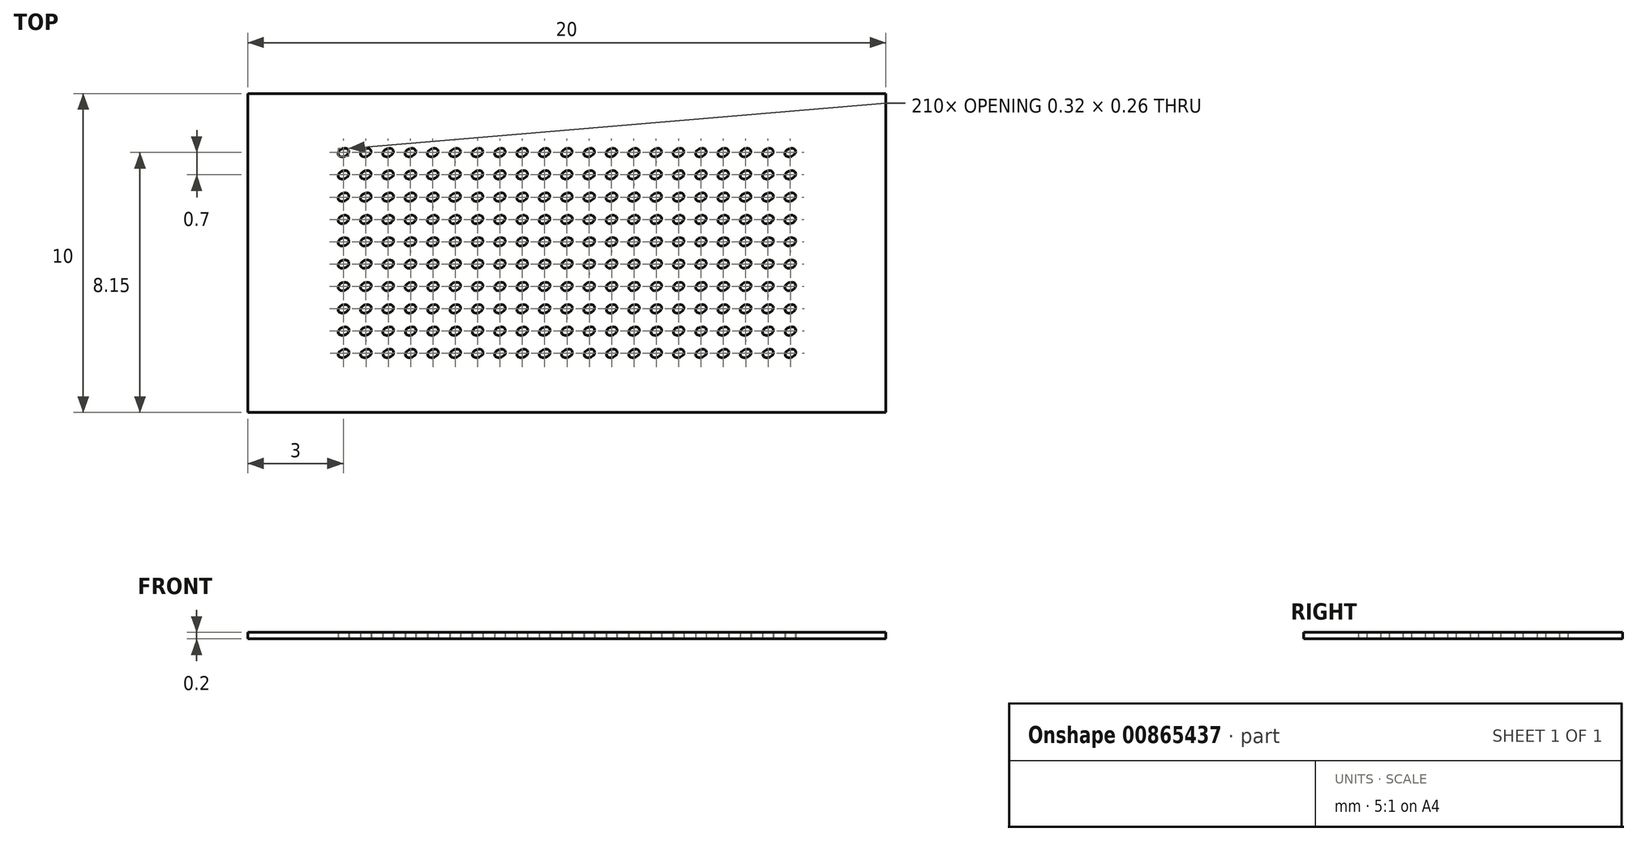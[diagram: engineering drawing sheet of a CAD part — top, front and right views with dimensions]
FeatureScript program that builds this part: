
annotation { "Feature Type Name" : "Feature", "Feature Type Description" : "" }
export const myFeature = defineFeature(function(context is Context, id is Id, definition is map)
    precondition{}
    {
        {
            var Q0;
            Q0=qCreatedBy(makeId("Top.planeOp"),FACE);
            var sketch = newSketch(context, id + "F0", { "sketchPlane" : qUnion([Q0])});
            skLineSegment(sketch, "E0.bottom", {"start": v(0, 0) * mm, "end": v(20, 0) * mm});
            skLineSegment(sketch, "E0.top", {"start": v(0, -10) * mm, "end": v(20, -10) * mm});
            skLineSegment(sketch, "E0.left", {"start": v(0, 0) * mm, "end": v(0, -10) * mm});
            skLineSegment(sketch, "E0.right", {"start": v(20, 0) * mm, "end": v(20, -10) * mm});
            skEllipse(sketch, "E1", {"center": v(3, -1.85) * mm, "majorRadius": 0.17 * mm, "minorRadius": 0.12 * mm, "majorAxis": v(0.93, 0.38)});
            skEllipse(sketch, "E2.1.0.0", {"center": v(3.7, -1.85) * mm, "majorRadius": 0.17 * mm, "minorRadius": 0.12 * mm, "majorAxis": v(0.93, 0.38)});
            skEllipse(sketch, "E2.2.0.0", {"center": v(4.4, -1.85) * mm, "majorRadius": 0.17 * mm, "minorRadius": 0.12 * mm, "majorAxis": v(0.93, 0.38)});
            skLineSegment(sketch, "E2.direction1", {"start": v(3, -1.85) * mm, "end": v(3.7, -1.85) * mm, "construction": true});
            skEllipse(sketch, "E3.0.3.0", {"center": v(5.1, -1.85) * mm, "majorRadius": 0.17 * mm, "minorRadius": 0.12 * mm, "majorAxis": v(0.93, 0.38)});
            skEllipse(sketch, "E3.0.4.0", {"center": v(5.8, -1.85) * mm, "majorRadius": 0.17 * mm, "minorRadius": 0.12 * mm, "majorAxis": v(0.93, 0.38)});
            skEllipse(sketch, "E3.0.5.0", {"center": v(6.5, -1.85) * mm, "majorRadius": 0.17 * mm, "minorRadius": 0.12 * mm, "majorAxis": v(0.93, 0.38)});
            skEllipse(sketch, "E3.0.6.0", {"center": v(7.2, -1.85) * mm, "majorRadius": 0.17 * mm, "minorRadius": 0.12 * mm, "majorAxis": v(0.93, 0.38)});
            skEllipse(sketch, "E3.0.7.0", {"center": v(7.9, -1.85) * mm, "majorRadius": 0.17 * mm, "minorRadius": 0.12 * mm, "majorAxis": v(0.93, 0.38)});
            skEllipse(sketch, "E3.0.8.0", {"center": v(8.6, -1.85) * mm, "majorRadius": 0.17 * mm, "minorRadius": 0.12 * mm, "majorAxis": v(0.93, 0.38)});
            skEllipse(sketch, "E3.0.9.0", {"center": v(9.3, -1.85) * mm, "majorRadius": 0.17 * mm, "minorRadius": 0.12 * mm, "majorAxis": v(0.93, 0.38)});
            skEllipse(sketch, "E3.0.10.0", {"center": v(10, -1.85) * mm, "majorRadius": 0.17 * mm, "minorRadius": 0.12 * mm, "majorAxis": v(0.93, 0.38)});
            skEllipse(sketch, "E3.0.11.0", {"center": v(10.7, -1.85) * mm, "majorRadius": 0.17 * mm, "minorRadius": 0.12 * mm, "majorAxis": v(0.93, 0.38)});
            skEllipse(sketch, "E3.0.12.0", {"center": v(11.4, -1.85) * mm, "majorRadius": 0.17 * mm, "minorRadius": 0.12 * mm, "majorAxis": v(0.93, 0.38)});
            skEllipse(sketch, "E3.0.13.0", {"center": v(12.1, -1.85) * mm, "majorRadius": 0.17 * mm, "minorRadius": 0.12 * mm, "majorAxis": v(0.93, 0.38)});
            skEllipse(sketch, "E3.0.14.0", {"center": v(12.8, -1.85) * mm, "majorRadius": 0.17 * mm, "minorRadius": 0.12 * mm, "majorAxis": v(0.93, 0.38)});
            skEllipse(sketch, "E3.0.15.0", {"center": v(13.5, -1.85) * mm, "majorRadius": 0.17 * mm, "minorRadius": 0.12 * mm, "majorAxis": v(0.93, 0.38)});
            skEllipse(sketch, "E3.0.16.0", {"center": v(14.2, -1.85) * mm, "majorRadius": 0.17 * mm, "minorRadius": 0.12 * mm, "majorAxis": v(0.93, 0.38)});
            skEllipse(sketch, "E3.0.17.0", {"center": v(14.9, -1.85) * mm, "majorRadius": 0.17 * mm, "minorRadius": 0.12 * mm, "majorAxis": v(0.93, 0.38)});
            skEllipse(sketch, "E3.0.18.0", {"center": v(15.6, -1.85) * mm, "majorRadius": 0.17 * mm, "minorRadius": 0.12 * mm, "majorAxis": v(0.93, 0.38)});
            skEllipse(sketch, "E3.0.19.0", {"center": v(16.3, -1.85) * mm, "majorRadius": 0.17 * mm, "minorRadius": 0.12 * mm, "majorAxis": v(0.93, 0.38)});
            skEllipse(sketch, "E4.0.20.0", {"center": v(17, -1.85) * mm, "majorRadius": 0.17 * mm, "minorRadius": 0.12 * mm, "majorAxis": v(0.93, 0.38)});
            skEllipse(sketch, "E5.1.0.0", {"center": v(17, -2.55) * mm, "majorRadius": 0.17 * mm, "minorRadius": 0.12 * mm, "majorAxis": v(0.93, 0.38)});
            skEllipse(sketch, "E5.1.0.1", {"center": v(16.3, -2.55) * mm, "majorRadius": 0.17 * mm, "minorRadius": 0.12 * mm, "majorAxis": v(0.93, 0.38)});
            skEllipse(sketch, "E5.1.0.2", {"center": v(15.6, -2.55) * mm, "majorRadius": 0.17 * mm, "minorRadius": 0.12 * mm, "majorAxis": v(0.93, 0.38)});
            skEllipse(sketch, "E5.1.0.3", {"center": v(14.9, -2.55) * mm, "majorRadius": 0.17 * mm, "minorRadius": 0.12 * mm, "majorAxis": v(0.93, 0.38)});
            skEllipse(sketch, "E5.1.0.4", {"center": v(14.2, -2.55) * mm, "majorRadius": 0.17 * mm, "minorRadius": 0.12 * mm, "majorAxis": v(0.93, 0.38)});
            skEllipse(sketch, "E5.1.0.5", {"center": v(13.5, -2.55) * mm, "majorRadius": 0.17 * mm, "minorRadius": 0.12 * mm, "majorAxis": v(0.93, 0.38)});
            skEllipse(sketch, "E5.1.0.6", {"center": v(12.8, -2.55) * mm, "majorRadius": 0.17 * mm, "minorRadius": 0.12 * mm, "majorAxis": v(0.93, 0.38)});
            skEllipse(sketch, "E5.1.0.7", {"center": v(12.1, -2.55) * mm, "majorRadius": 0.17 * mm, "minorRadius": 0.12 * mm, "majorAxis": v(0.93, 0.38)});
            skEllipse(sketch, "E5.1.0.8", {"center": v(11.4, -2.55) * mm, "majorRadius": 0.17 * mm, "minorRadius": 0.12 * mm, "majorAxis": v(0.93, 0.38)});
            skEllipse(sketch, "E5.1.0.9", {"center": v(10.7, -2.55) * mm, "majorRadius": 0.17 * mm, "minorRadius": 0.12 * mm, "majorAxis": v(0.93, 0.38)});
            skEllipse(sketch, "E5.1.0.10", {"center": v(10, -2.55) * mm, "majorRadius": 0.17 * mm, "minorRadius": 0.12 * mm, "majorAxis": v(0.93, 0.38)});
            skEllipse(sketch, "E5.1.0.11", {"center": v(9.3, -2.55) * mm, "majorRadius": 0.17 * mm, "minorRadius": 0.12 * mm, "majorAxis": v(0.93, 0.38)});
            skEllipse(sketch, "E5.1.0.12", {"center": v(8.6, -2.55) * mm, "majorRadius": 0.17 * mm, "minorRadius": 0.12 * mm, "majorAxis": v(0.93, 0.38)});
            skEllipse(sketch, "E5.1.0.13", {"center": v(7.9, -2.55) * mm, "majorRadius": 0.17 * mm, "minorRadius": 0.12 * mm, "majorAxis": v(0.93, 0.38)});
            skEllipse(sketch, "E5.1.0.14", {"center": v(7.2, -2.55) * mm, "majorRadius": 0.17 * mm, "minorRadius": 0.12 * mm, "majorAxis": v(0.93, 0.38)});
            skEllipse(sketch, "E5.1.0.15", {"center": v(5.8, -2.55) * mm, "majorRadius": 0.17 * mm, "minorRadius": 0.12 * mm, "majorAxis": v(0.93, 0.38)});
            skEllipse(sketch, "E5.1.0.16", {"center": v(5.1, -2.55) * mm, "majorRadius": 0.17 * mm, "minorRadius": 0.12 * mm, "majorAxis": v(0.93, 0.38)});
            skEllipse(sketch, "E5.1.0.17", {"center": v(6.5, -2.55) * mm, "majorRadius": 0.17 * mm, "minorRadius": 0.12 * mm, "majorAxis": v(0.93, 0.38)});
            skEllipse(sketch, "E5.1.0.18", {"center": v(4.4, -2.55) * mm, "majorRadius": 0.17 * mm, "minorRadius": 0.12 * mm, "majorAxis": v(0.93, 0.38)});
            skEllipse(sketch, "E5.1.0.19", {"center": v(3.7, -2.55) * mm, "majorRadius": 0.17 * mm, "minorRadius": 0.12 * mm, "majorAxis": v(0.93, 0.38)});
            skEllipse(sketch, "E5.1.0.20", {"center": v(3, -2.55) * mm, "majorRadius": 0.17 * mm, "minorRadius": 0.12 * mm, "majorAxis": v(0.93, 0.38)});
            skEllipse(sketch, "E5.2.0.0", {"center": v(17, -3.25) * mm, "majorRadius": 0.17 * mm, "minorRadius": 0.12 * mm, "majorAxis": v(0.93, 0.38)});
            skEllipse(sketch, "E5.2.0.1", {"center": v(16.3, -3.25) * mm, "majorRadius": 0.17 * mm, "minorRadius": 0.12 * mm, "majorAxis": v(0.93, 0.38)});
            skEllipse(sketch, "E5.2.0.2", {"center": v(15.6, -3.25) * mm, "majorRadius": 0.17 * mm, "minorRadius": 0.12 * mm, "majorAxis": v(0.93, 0.38)});
            skEllipse(sketch, "E5.2.0.3", {"center": v(14.9, -3.25) * mm, "majorRadius": 0.17 * mm, "minorRadius": 0.12 * mm, "majorAxis": v(0.93, 0.38)});
            skEllipse(sketch, "E5.2.0.4", {"center": v(14.2, -3.25) * mm, "majorRadius": 0.17 * mm, "minorRadius": 0.12 * mm, "majorAxis": v(0.93, 0.38)});
            skEllipse(sketch, "E5.2.0.5", {"center": v(13.5, -3.25) * mm, "majorRadius": 0.17 * mm, "minorRadius": 0.12 * mm, "majorAxis": v(0.93, 0.38)});
            skEllipse(sketch, "E5.2.0.6", {"center": v(12.8, -3.25) * mm, "majorRadius": 0.17 * mm, "minorRadius": 0.12 * mm, "majorAxis": v(0.93, 0.38)});
            skEllipse(sketch, "E5.2.0.7", {"center": v(12.1, -3.25) * mm, "majorRadius": 0.17 * mm, "minorRadius": 0.12 * mm, "majorAxis": v(0.93, 0.38)});
            skEllipse(sketch, "E5.2.0.8", {"center": v(11.4, -3.25) * mm, "majorRadius": 0.17 * mm, "minorRadius": 0.12 * mm, "majorAxis": v(0.93, 0.38)});
            skEllipse(sketch, "E5.2.0.9", {"center": v(10.7, -3.25) * mm, "majorRadius": 0.17 * mm, "minorRadius": 0.12 * mm, "majorAxis": v(0.93, 0.38)});
            skEllipse(sketch, "E5.2.0.10", {"center": v(10, -3.25) * mm, "majorRadius": 0.17 * mm, "minorRadius": 0.12 * mm, "majorAxis": v(0.93, 0.38)});
            skEllipse(sketch, "E5.2.0.11", {"center": v(9.3, -3.25) * mm, "majorRadius": 0.17 * mm, "minorRadius": 0.12 * mm, "majorAxis": v(0.93, 0.38)});
            skEllipse(sketch, "E5.2.0.12", {"center": v(8.6, -3.25) * mm, "majorRadius": 0.17 * mm, "minorRadius": 0.12 * mm, "majorAxis": v(0.93, 0.38)});
            skEllipse(sketch, "E5.2.0.13", {"center": v(7.9, -3.25) * mm, "majorRadius": 0.17 * mm, "minorRadius": 0.12 * mm, "majorAxis": v(0.93, 0.38)});
            skEllipse(sketch, "E5.2.0.14", {"center": v(7.2, -3.25) * mm, "majorRadius": 0.17 * mm, "minorRadius": 0.12 * mm, "majorAxis": v(0.93, 0.38)});
            skEllipse(sketch, "E5.2.0.15", {"center": v(5.8, -3.25) * mm, "majorRadius": 0.17 * mm, "minorRadius": 0.12 * mm, "majorAxis": v(0.93, 0.38)});
            skEllipse(sketch, "E5.2.0.16", {"center": v(5.1, -3.25) * mm, "majorRadius": 0.17 * mm, "minorRadius": 0.12 * mm, "majorAxis": v(0.93, 0.38)});
            skEllipse(sketch, "E5.2.0.17", {"center": v(6.5, -3.25) * mm, "majorRadius": 0.17 * mm, "minorRadius": 0.12 * mm, "majorAxis": v(0.93, 0.38)});
            skEllipse(sketch, "E5.2.0.18", {"center": v(4.4, -3.25) * mm, "majorRadius": 0.17 * mm, "minorRadius": 0.12 * mm, "majorAxis": v(0.93, 0.38)});
            skEllipse(sketch, "E5.2.0.19", {"center": v(3.7, -3.25) * mm, "majorRadius": 0.17 * mm, "minorRadius": 0.12 * mm, "majorAxis": v(0.93, 0.38)});
            skEllipse(sketch, "E5.2.0.20", {"center": v(3, -3.25) * mm, "majorRadius": 0.17 * mm, "minorRadius": 0.12 * mm, "majorAxis": v(0.93, 0.38)});
            skEllipse(sketch, "E5.3.0.0", {"center": v(17, -3.95) * mm, "majorRadius": 0.17 * mm, "minorRadius": 0.12 * mm, "majorAxis": v(0.93, 0.38)});
            skEllipse(sketch, "E5.3.0.1", {"center": v(16.3, -3.95) * mm, "majorRadius": 0.17 * mm, "minorRadius": 0.12 * mm, "majorAxis": v(0.93, 0.38)});
            skEllipse(sketch, "E5.3.0.2", {"center": v(15.6, -3.95) * mm, "majorRadius": 0.17 * mm, "minorRadius": 0.12 * mm, "majorAxis": v(0.93, 0.38)});
            skEllipse(sketch, "E5.3.0.3", {"center": v(14.9, -3.95) * mm, "majorRadius": 0.17 * mm, "minorRadius": 0.12 * mm, "majorAxis": v(0.93, 0.38)});
            skEllipse(sketch, "E5.3.0.4", {"center": v(14.2, -3.95) * mm, "majorRadius": 0.17 * mm, "minorRadius": 0.12 * mm, "majorAxis": v(0.93, 0.38)});
            skEllipse(sketch, "E5.3.0.5", {"center": v(13.5, -3.95) * mm, "majorRadius": 0.17 * mm, "minorRadius": 0.12 * mm, "majorAxis": v(0.93, 0.38)});
            skEllipse(sketch, "E5.3.0.6", {"center": v(12.8, -3.95) * mm, "majorRadius": 0.17 * mm, "minorRadius": 0.12 * mm, "majorAxis": v(0.93, 0.38)});
            skEllipse(sketch, "E5.3.0.7", {"center": v(12.1, -3.95) * mm, "majorRadius": 0.17 * mm, "minorRadius": 0.12 * mm, "majorAxis": v(0.93, 0.38)});
            skEllipse(sketch, "E5.3.0.8", {"center": v(11.4, -3.95) * mm, "majorRadius": 0.17 * mm, "minorRadius": 0.12 * mm, "majorAxis": v(0.93, 0.38)});
            skEllipse(sketch, "E5.3.0.9", {"center": v(10.7, -3.95) * mm, "majorRadius": 0.17 * mm, "minorRadius": 0.12 * mm, "majorAxis": v(0.93, 0.38)});
            skEllipse(sketch, "E5.3.0.10", {"center": v(10, -3.95) * mm, "majorRadius": 0.17 * mm, "minorRadius": 0.12 * mm, "majorAxis": v(0.93, 0.38)});
            skEllipse(sketch, "E5.3.0.11", {"center": v(9.3, -3.95) * mm, "majorRadius": 0.17 * mm, "minorRadius": 0.12 * mm, "majorAxis": v(0.93, 0.38)});
            skEllipse(sketch, "E5.3.0.12", {"center": v(8.6, -3.95) * mm, "majorRadius": 0.17 * mm, "minorRadius": 0.12 * mm, "majorAxis": v(0.93, 0.38)});
            skEllipse(sketch, "E5.3.0.13", {"center": v(7.9, -3.95) * mm, "majorRadius": 0.17 * mm, "minorRadius": 0.12 * mm, "majorAxis": v(0.93, 0.38)});
            skEllipse(sketch, "E5.3.0.14", {"center": v(7.2, -3.95) * mm, "majorRadius": 0.17 * mm, "minorRadius": 0.12 * mm, "majorAxis": v(0.93, 0.38)});
            skEllipse(sketch, "E5.3.0.15", {"center": v(5.8, -3.95) * mm, "majorRadius": 0.17 * mm, "minorRadius": 0.12 * mm, "majorAxis": v(0.93, 0.38)});
            skEllipse(sketch, "E5.3.0.16", {"center": v(5.1, -3.95) * mm, "majorRadius": 0.17 * mm, "minorRadius": 0.12 * mm, "majorAxis": v(0.93, 0.38)});
            skEllipse(sketch, "E5.3.0.17", {"center": v(6.5, -3.95) * mm, "majorRadius": 0.17 * mm, "minorRadius": 0.12 * mm, "majorAxis": v(0.93, 0.38)});
            skEllipse(sketch, "E5.3.0.18", {"center": v(4.4, -3.95) * mm, "majorRadius": 0.17 * mm, "minorRadius": 0.12 * mm, "majorAxis": v(0.93, 0.38)});
            skEllipse(sketch, "E5.3.0.19", {"center": v(3.7, -3.95) * mm, "majorRadius": 0.17 * mm, "minorRadius": 0.12 * mm, "majorAxis": v(0.93, 0.38)});
            skEllipse(sketch, "E5.3.0.20", {"center": v(3, -3.95) * mm, "majorRadius": 0.17 * mm, "minorRadius": 0.12 * mm, "majorAxis": v(0.93, 0.38)});
            skEllipse(sketch, "E5.4.0.0", {"center": v(17, -4.65) * mm, "majorRadius": 0.17 * mm, "minorRadius": 0.12 * mm, "majorAxis": v(0.93, 0.38)});
            skEllipse(sketch, "E5.4.0.1", {"center": v(16.3, -4.65) * mm, "majorRadius": 0.17 * mm, "minorRadius": 0.12 * mm, "majorAxis": v(0.93, 0.38)});
            skEllipse(sketch, "E5.4.0.2", {"center": v(15.6, -4.65) * mm, "majorRadius": 0.17 * mm, "minorRadius": 0.12 * mm, "majorAxis": v(0.93, 0.38)});
            skEllipse(sketch, "E5.4.0.3", {"center": v(14.9, -4.65) * mm, "majorRadius": 0.17 * mm, "minorRadius": 0.12 * mm, "majorAxis": v(0.93, 0.38)});
            skEllipse(sketch, "E5.4.0.4", {"center": v(14.2, -4.65) * mm, "majorRadius": 0.17 * mm, "minorRadius": 0.12 * mm, "majorAxis": v(0.93, 0.38)});
            skEllipse(sketch, "E5.4.0.5", {"center": v(13.5, -4.65) * mm, "majorRadius": 0.17 * mm, "minorRadius": 0.12 * mm, "majorAxis": v(0.93, 0.38)});
            skEllipse(sketch, "E5.4.0.6", {"center": v(12.8, -4.65) * mm, "majorRadius": 0.17 * mm, "minorRadius": 0.12 * mm, "majorAxis": v(0.93, 0.38)});
            skEllipse(sketch, "E5.4.0.7", {"center": v(12.1, -4.65) * mm, "majorRadius": 0.17 * mm, "minorRadius": 0.12 * mm, "majorAxis": v(0.93, 0.38)});
            skEllipse(sketch, "E5.4.0.8", {"center": v(11.4, -4.65) * mm, "majorRadius": 0.17 * mm, "minorRadius": 0.12 * mm, "majorAxis": v(0.93, 0.38)});
            skEllipse(sketch, "E5.4.0.9", {"center": v(10.7, -4.65) * mm, "majorRadius": 0.17 * mm, "minorRadius": 0.12 * mm, "majorAxis": v(0.93, 0.38)});
            skEllipse(sketch, "E5.4.0.10", {"center": v(10, -4.65) * mm, "majorRadius": 0.17 * mm, "minorRadius": 0.12 * mm, "majorAxis": v(0.93, 0.38)});
            skEllipse(sketch, "E5.4.0.11", {"center": v(9.3, -4.65) * mm, "majorRadius": 0.17 * mm, "minorRadius": 0.12 * mm, "majorAxis": v(0.93, 0.38)});
            skEllipse(sketch, "E5.4.0.12", {"center": v(8.6, -4.65) * mm, "majorRadius": 0.17 * mm, "minorRadius": 0.12 * mm, "majorAxis": v(0.93, 0.38)});
            skEllipse(sketch, "E5.4.0.13", {"center": v(7.9, -4.65) * mm, "majorRadius": 0.17 * mm, "minorRadius": 0.12 * mm, "majorAxis": v(0.93, 0.38)});
            skEllipse(sketch, "E5.4.0.14", {"center": v(7.2, -4.65) * mm, "majorRadius": 0.17 * mm, "minorRadius": 0.12 * mm, "majorAxis": v(0.93, 0.38)});
            skEllipse(sketch, "E5.4.0.15", {"center": v(5.8, -4.65) * mm, "majorRadius": 0.17 * mm, "minorRadius": 0.12 * mm, "majorAxis": v(0.93, 0.38)});
            skEllipse(sketch, "E5.4.0.16", {"center": v(5.1, -4.65) * mm, "majorRadius": 0.17 * mm, "minorRadius": 0.12 * mm, "majorAxis": v(0.93, 0.38)});
            skEllipse(sketch, "E5.4.0.17", {"center": v(6.5, -4.65) * mm, "majorRadius": 0.17 * mm, "minorRadius": 0.12 * mm, "majorAxis": v(0.93, 0.38)});
            skEllipse(sketch, "E5.4.0.18", {"center": v(4.4, -4.65) * mm, "majorRadius": 0.17 * mm, "minorRadius": 0.12 * mm, "majorAxis": v(0.93, 0.38)});
            skEllipse(sketch, "E5.4.0.19", {"center": v(3.7, -4.65) * mm, "majorRadius": 0.17 * mm, "minorRadius": 0.12 * mm, "majorAxis": v(0.93, 0.38)});
            skEllipse(sketch, "E5.4.0.20", {"center": v(3, -4.65) * mm, "majorRadius": 0.17 * mm, "minorRadius": 0.12 * mm, "majorAxis": v(0.93, 0.38)});
            skEllipse(sketch, "E5.5.0.0", {"center": v(17, -5.35) * mm, "majorRadius": 0.17 * mm, "minorRadius": 0.12 * mm, "majorAxis": v(0.93, 0.38)});
            skEllipse(sketch, "E5.5.0.1", {"center": v(16.3, -5.35) * mm, "majorRadius": 0.17 * mm, "minorRadius": 0.12 * mm, "majorAxis": v(0.93, 0.38)});
            skEllipse(sketch, "E5.5.0.2", {"center": v(15.6, -5.35) * mm, "majorRadius": 0.17 * mm, "minorRadius": 0.12 * mm, "majorAxis": v(0.93, 0.38)});
            skEllipse(sketch, "E5.5.0.3", {"center": v(14.9, -5.35) * mm, "majorRadius": 0.17 * mm, "minorRadius": 0.12 * mm, "majorAxis": v(0.93, 0.38)});
            skEllipse(sketch, "E5.5.0.4", {"center": v(14.2, -5.35) * mm, "majorRadius": 0.17 * mm, "minorRadius": 0.12 * mm, "majorAxis": v(0.93, 0.38)});
            skEllipse(sketch, "E5.5.0.5", {"center": v(13.5, -5.35) * mm, "majorRadius": 0.17 * mm, "minorRadius": 0.12 * mm, "majorAxis": v(0.93, 0.38)});
            skEllipse(sketch, "E5.5.0.6", {"center": v(12.8, -5.35) * mm, "majorRadius": 0.17 * mm, "minorRadius": 0.12 * mm, "majorAxis": v(0.93, 0.38)});
            skEllipse(sketch, "E5.5.0.7", {"center": v(12.1, -5.35) * mm, "majorRadius": 0.17 * mm, "minorRadius": 0.12 * mm, "majorAxis": v(0.93, 0.38)});
            skEllipse(sketch, "E5.5.0.8", {"center": v(11.4, -5.35) * mm, "majorRadius": 0.17 * mm, "minorRadius": 0.12 * mm, "majorAxis": v(0.93, 0.38)});
            skEllipse(sketch, "E5.5.0.9", {"center": v(10.7, -5.35) * mm, "majorRadius": 0.17 * mm, "minorRadius": 0.12 * mm, "majorAxis": v(0.93, 0.38)});
            skEllipse(sketch, "E5.5.0.10", {"center": v(10, -5.35) * mm, "majorRadius": 0.17 * mm, "minorRadius": 0.12 * mm, "majorAxis": v(0.93, 0.38)});
            skEllipse(sketch, "E5.5.0.11", {"center": v(9.3, -5.35) * mm, "majorRadius": 0.17 * mm, "minorRadius": 0.12 * mm, "majorAxis": v(0.93, 0.38)});
            skEllipse(sketch, "E5.5.0.12", {"center": v(8.6, -5.35) * mm, "majorRadius": 0.17 * mm, "minorRadius": 0.12 * mm, "majorAxis": v(0.93, 0.38)});
            skEllipse(sketch, "E5.5.0.13", {"center": v(7.9, -5.35) * mm, "majorRadius": 0.17 * mm, "minorRadius": 0.12 * mm, "majorAxis": v(0.93, 0.38)});
            skEllipse(sketch, "E5.5.0.14", {"center": v(7.2, -5.35) * mm, "majorRadius": 0.17 * mm, "minorRadius": 0.12 * mm, "majorAxis": v(0.93, 0.38)});
            skEllipse(sketch, "E5.5.0.15", {"center": v(5.8, -5.35) * mm, "majorRadius": 0.17 * mm, "minorRadius": 0.12 * mm, "majorAxis": v(0.93, 0.38)});
            skEllipse(sketch, "E5.5.0.16", {"center": v(5.1, -5.35) * mm, "majorRadius": 0.17 * mm, "minorRadius": 0.12 * mm, "majorAxis": v(0.93, 0.38)});
            skEllipse(sketch, "E5.5.0.17", {"center": v(6.5, -5.35) * mm, "majorRadius": 0.17 * mm, "minorRadius": 0.12 * mm, "majorAxis": v(0.93, 0.38)});
            skEllipse(sketch, "E5.5.0.18", {"center": v(4.4, -5.35) * mm, "majorRadius": 0.17 * mm, "minorRadius": 0.12 * mm, "majorAxis": v(0.93, 0.38)});
            skEllipse(sketch, "E5.5.0.19", {"center": v(3.7, -5.35) * mm, "majorRadius": 0.17 * mm, "minorRadius": 0.12 * mm, "majorAxis": v(0.93, 0.38)});
            skEllipse(sketch, "E5.5.0.20", {"center": v(3, -5.35) * mm, "majorRadius": 0.17 * mm, "minorRadius": 0.12 * mm, "majorAxis": v(0.93, 0.38)});
            skEllipse(sketch, "E5.6.0.0", {"center": v(17, -6.05) * mm, "majorRadius": 0.17 * mm, "minorRadius": 0.12 * mm, "majorAxis": v(0.93, 0.38)});
            skEllipse(sketch, "E5.6.0.1", {"center": v(16.3, -6.05) * mm, "majorRadius": 0.17 * mm, "minorRadius": 0.12 * mm, "majorAxis": v(0.93, 0.38)});
            skEllipse(sketch, "E5.6.0.2", {"center": v(15.6, -6.05) * mm, "majorRadius": 0.17 * mm, "minorRadius": 0.12 * mm, "majorAxis": v(0.93, 0.38)});
            skEllipse(sketch, "E5.6.0.3", {"center": v(14.9, -6.05) * mm, "majorRadius": 0.17 * mm, "minorRadius": 0.12 * mm, "majorAxis": v(0.93, 0.38)});
            skEllipse(sketch, "E5.6.0.4", {"center": v(14.2, -6.05) * mm, "majorRadius": 0.17 * mm, "minorRadius": 0.12 * mm, "majorAxis": v(0.93, 0.38)});
            skEllipse(sketch, "E5.6.0.5", {"center": v(13.5, -6.05) * mm, "majorRadius": 0.17 * mm, "minorRadius": 0.12 * mm, "majorAxis": v(0.93, 0.38)});
            skEllipse(sketch, "E5.6.0.6", {"center": v(12.8, -6.05) * mm, "majorRadius": 0.17 * mm, "minorRadius": 0.12 * mm, "majorAxis": v(0.93, 0.38)});
            skEllipse(sketch, "E5.6.0.7", {"center": v(12.1, -6.05) * mm, "majorRadius": 0.17 * mm, "minorRadius": 0.12 * mm, "majorAxis": v(0.93, 0.38)});
            skEllipse(sketch, "E5.6.0.8", {"center": v(11.4, -6.05) * mm, "majorRadius": 0.17 * mm, "minorRadius": 0.12 * mm, "majorAxis": v(0.93, 0.38)});
            skEllipse(sketch, "E5.6.0.9", {"center": v(10.7, -6.05) * mm, "majorRadius": 0.17 * mm, "minorRadius": 0.12 * mm, "majorAxis": v(0.93, 0.38)});
            skEllipse(sketch, "E5.6.0.10", {"center": v(10, -6.05) * mm, "majorRadius": 0.17 * mm, "minorRadius": 0.12 * mm, "majorAxis": v(0.93, 0.38)});
            skEllipse(sketch, "E5.6.0.11", {"center": v(9.3, -6.05) * mm, "majorRadius": 0.17 * mm, "minorRadius": 0.12 * mm, "majorAxis": v(0.93, 0.38)});
            skEllipse(sketch, "E5.6.0.12", {"center": v(8.6, -6.05) * mm, "majorRadius": 0.17 * mm, "minorRadius": 0.12 * mm, "majorAxis": v(0.93, 0.38)});
            skEllipse(sketch, "E5.6.0.13", {"center": v(7.9, -6.05) * mm, "majorRadius": 0.17 * mm, "minorRadius": 0.12 * mm, "majorAxis": v(0.93, 0.38)});
            skEllipse(sketch, "E5.6.0.14", {"center": v(7.2, -6.05) * mm, "majorRadius": 0.17 * mm, "minorRadius": 0.12 * mm, "majorAxis": v(0.93, 0.38)});
            skEllipse(sketch, "E5.6.0.15", {"center": v(5.8, -6.05) * mm, "majorRadius": 0.17 * mm, "minorRadius": 0.12 * mm, "majorAxis": v(0.93, 0.38)});
            skEllipse(sketch, "E5.6.0.16", {"center": v(5.1, -6.05) * mm, "majorRadius": 0.17 * mm, "minorRadius": 0.12 * mm, "majorAxis": v(0.93, 0.38)});
            skEllipse(sketch, "E5.6.0.17", {"center": v(6.5, -6.05) * mm, "majorRadius": 0.17 * mm, "minorRadius": 0.12 * mm, "majorAxis": v(0.93, 0.38)});
            skEllipse(sketch, "E5.6.0.18", {"center": v(4.4, -6.05) * mm, "majorRadius": 0.17 * mm, "minorRadius": 0.12 * mm, "majorAxis": v(0.93, 0.38)});
            skEllipse(sketch, "E5.6.0.19", {"center": v(3.7, -6.05) * mm, "majorRadius": 0.17 * mm, "minorRadius": 0.12 * mm, "majorAxis": v(0.93, 0.38)});
            skEllipse(sketch, "E5.6.0.20", {"center": v(3, -6.05) * mm, "majorRadius": 0.17 * mm, "minorRadius": 0.12 * mm, "majorAxis": v(0.93, 0.38)});
            skEllipse(sketch, "E5.7.0.0", {"center": v(17, -6.75) * mm, "majorRadius": 0.17 * mm, "minorRadius": 0.12 * mm, "majorAxis": v(0.93, 0.38)});
            skEllipse(sketch, "E5.7.0.1", {"center": v(16.3, -6.75) * mm, "majorRadius": 0.17 * mm, "minorRadius": 0.12 * mm, "majorAxis": v(0.93, 0.38)});
            skEllipse(sketch, "E5.7.0.2", {"center": v(15.6, -6.75) * mm, "majorRadius": 0.17 * mm, "minorRadius": 0.12 * mm, "majorAxis": v(0.93, 0.38)});
            skEllipse(sketch, "E5.7.0.3", {"center": v(14.9, -6.75) * mm, "majorRadius": 0.17 * mm, "minorRadius": 0.12 * mm, "majorAxis": v(0.93, 0.38)});
            skEllipse(sketch, "E5.7.0.4", {"center": v(14.2, -6.75) * mm, "majorRadius": 0.17 * mm, "minorRadius": 0.12 * mm, "majorAxis": v(0.93, 0.38)});
            skEllipse(sketch, "E5.7.0.5", {"center": v(13.5, -6.75) * mm, "majorRadius": 0.17 * mm, "minorRadius": 0.12 * mm, "majorAxis": v(0.93, 0.38)});
            skEllipse(sketch, "E5.7.0.6", {"center": v(12.8, -6.75) * mm, "majorRadius": 0.17 * mm, "minorRadius": 0.12 * mm, "majorAxis": v(0.93, 0.38)});
            skEllipse(sketch, "E5.7.0.7", {"center": v(12.1, -6.75) * mm, "majorRadius": 0.17 * mm, "minorRadius": 0.12 * mm, "majorAxis": v(0.93, 0.38)});
            skEllipse(sketch, "E5.7.0.8", {"center": v(11.4, -6.75) * mm, "majorRadius": 0.17 * mm, "minorRadius": 0.12 * mm, "majorAxis": v(0.93, 0.38)});
            skEllipse(sketch, "E5.7.0.9", {"center": v(10.7, -6.75) * mm, "majorRadius": 0.17 * mm, "minorRadius": 0.12 * mm, "majorAxis": v(0.93, 0.38)});
            skEllipse(sketch, "E5.7.0.10", {"center": v(10, -6.75) * mm, "majorRadius": 0.17 * mm, "minorRadius": 0.12 * mm, "majorAxis": v(0.93, 0.38)});
            skEllipse(sketch, "E5.7.0.11", {"center": v(9.3, -6.75) * mm, "majorRadius": 0.17 * mm, "minorRadius": 0.12 * mm, "majorAxis": v(0.93, 0.38)});
            skEllipse(sketch, "E5.7.0.12", {"center": v(8.6, -6.75) * mm, "majorRadius": 0.17 * mm, "minorRadius": 0.12 * mm, "majorAxis": v(0.93, 0.38)});
            skEllipse(sketch, "E5.7.0.13", {"center": v(7.9, -6.75) * mm, "majorRadius": 0.17 * mm, "minorRadius": 0.12 * mm, "majorAxis": v(0.93, 0.38)});
            skEllipse(sketch, "E5.7.0.14", {"center": v(7.2, -6.75) * mm, "majorRadius": 0.17 * mm, "minorRadius": 0.12 * mm, "majorAxis": v(0.93, 0.38)});
            skEllipse(sketch, "E5.7.0.15", {"center": v(5.8, -6.75) * mm, "majorRadius": 0.17 * mm, "minorRadius": 0.12 * mm, "majorAxis": v(0.93, 0.38)});
            skEllipse(sketch, "E5.7.0.16", {"center": v(5.1, -6.75) * mm, "majorRadius": 0.17 * mm, "minorRadius": 0.12 * mm, "majorAxis": v(0.93, 0.38)});
            skEllipse(sketch, "E5.7.0.17", {"center": v(6.5, -6.75) * mm, "majorRadius": 0.17 * mm, "minorRadius": 0.12 * mm, "majorAxis": v(0.93, 0.38)});
            skEllipse(sketch, "E5.7.0.18", {"center": v(4.4, -6.75) * mm, "majorRadius": 0.17 * mm, "minorRadius": 0.12 * mm, "majorAxis": v(0.93, 0.38)});
            skEllipse(sketch, "E5.7.0.19", {"center": v(3.7, -6.75) * mm, "majorRadius": 0.17 * mm, "minorRadius": 0.12 * mm, "majorAxis": v(0.93, 0.38)});
            skEllipse(sketch, "E5.7.0.20", {"center": v(3, -6.75) * mm, "majorRadius": 0.17 * mm, "minorRadius": 0.12 * mm, "majorAxis": v(0.93, 0.38)});
            skEllipse(sketch, "E5.8.0.0", {"center": v(17, -7.45) * mm, "majorRadius": 0.17 * mm, "minorRadius": 0.12 * mm, "majorAxis": v(0.93, 0.38)});
            skEllipse(sketch, "E5.8.0.1", {"center": v(16.3, -7.45) * mm, "majorRadius": 0.17 * mm, "minorRadius": 0.12 * mm, "majorAxis": v(0.93, 0.38)});
            skEllipse(sketch, "E5.8.0.2", {"center": v(15.6, -7.45) * mm, "majorRadius": 0.17 * mm, "minorRadius": 0.12 * mm, "majorAxis": v(0.93, 0.38)});
            skEllipse(sketch, "E5.8.0.3", {"center": v(14.9, -7.45) * mm, "majorRadius": 0.17 * mm, "minorRadius": 0.12 * mm, "majorAxis": v(0.93, 0.38)});
            skEllipse(sketch, "E5.8.0.4", {"center": v(14.2, -7.45) * mm, "majorRadius": 0.17 * mm, "minorRadius": 0.12 * mm, "majorAxis": v(0.93, 0.38)});
            skEllipse(sketch, "E5.8.0.5", {"center": v(13.5, -7.45) * mm, "majorRadius": 0.17 * mm, "minorRadius": 0.12 * mm, "majorAxis": v(0.93, 0.38)});
            skEllipse(sketch, "E5.8.0.6", {"center": v(12.8, -7.45) * mm, "majorRadius": 0.17 * mm, "minorRadius": 0.12 * mm, "majorAxis": v(0.93, 0.38)});
            skEllipse(sketch, "E5.8.0.7", {"center": v(12.1, -7.45) * mm, "majorRadius": 0.17 * mm, "minorRadius": 0.12 * mm, "majorAxis": v(0.93, 0.38)});
            skEllipse(sketch, "E5.8.0.8", {"center": v(11.4, -7.45) * mm, "majorRadius": 0.17 * mm, "minorRadius": 0.12 * mm, "majorAxis": v(0.93, 0.38)});
            skEllipse(sketch, "E5.8.0.9", {"center": v(10.7, -7.45) * mm, "majorRadius": 0.17 * mm, "minorRadius": 0.12 * mm, "majorAxis": v(0.93, 0.38)});
            skEllipse(sketch, "E5.8.0.10", {"center": v(10, -7.45) * mm, "majorRadius": 0.17 * mm, "minorRadius": 0.12 * mm, "majorAxis": v(0.93, 0.38)});
            skEllipse(sketch, "E5.8.0.11", {"center": v(9.3, -7.45) * mm, "majorRadius": 0.17 * mm, "minorRadius": 0.12 * mm, "majorAxis": v(0.93, 0.38)});
            skEllipse(sketch, "E5.8.0.12", {"center": v(8.6, -7.45) * mm, "majorRadius": 0.17 * mm, "minorRadius": 0.12 * mm, "majorAxis": v(0.93, 0.38)});
            skEllipse(sketch, "E5.8.0.13", {"center": v(7.9, -7.45) * mm, "majorRadius": 0.17 * mm, "minorRadius": 0.12 * mm, "majorAxis": v(0.93, 0.38)});
            skEllipse(sketch, "E5.8.0.14", {"center": v(7.2, -7.45) * mm, "majorRadius": 0.17 * mm, "minorRadius": 0.12 * mm, "majorAxis": v(0.93, 0.38)});
            skEllipse(sketch, "E5.8.0.15", {"center": v(5.8, -7.45) * mm, "majorRadius": 0.17 * mm, "minorRadius": 0.12 * mm, "majorAxis": v(0.93, 0.38)});
            skEllipse(sketch, "E5.8.0.16", {"center": v(5.1, -7.45) * mm, "majorRadius": 0.17 * mm, "minorRadius": 0.12 * mm, "majorAxis": v(0.93, 0.38)});
            skEllipse(sketch, "E5.8.0.17", {"center": v(6.5, -7.45) * mm, "majorRadius": 0.17 * mm, "minorRadius": 0.12 * mm, "majorAxis": v(0.93, 0.38)});
            skEllipse(sketch, "E5.8.0.18", {"center": v(4.4, -7.45) * mm, "majorRadius": 0.17 * mm, "minorRadius": 0.12 * mm, "majorAxis": v(0.93, 0.38)});
            skEllipse(sketch, "E5.8.0.19", {"center": v(3.7, -7.45) * mm, "majorRadius": 0.17 * mm, "minorRadius": 0.12 * mm, "majorAxis": v(0.93, 0.38)});
            skEllipse(sketch, "E5.8.0.20", {"center": v(3, -7.45) * mm, "majorRadius": 0.17 * mm, "minorRadius": 0.12 * mm, "majorAxis": v(0.93, 0.38)});
            skEllipse(sketch, "E5.9.0.0", {"center": v(17, -8.15) * mm, "majorRadius": 0.17 * mm, "minorRadius": 0.12 * mm, "majorAxis": v(0.93, 0.38)});
            skEllipse(sketch, "E5.9.0.1", {"center": v(16.3, -8.15) * mm, "majorRadius": 0.17 * mm, "minorRadius": 0.12 * mm, "majorAxis": v(0.93, 0.38)});
            skEllipse(sketch, "E5.9.0.2", {"center": v(15.6, -8.15) * mm, "majorRadius": 0.17 * mm, "minorRadius": 0.12 * mm, "majorAxis": v(0.93, 0.38)});
            skEllipse(sketch, "E5.9.0.3", {"center": v(14.9, -8.15) * mm, "majorRadius": 0.17 * mm, "minorRadius": 0.12 * mm, "majorAxis": v(0.93, 0.38)});
            skEllipse(sketch, "E5.9.0.4", {"center": v(14.2, -8.15) * mm, "majorRadius": 0.17 * mm, "minorRadius": 0.12 * mm, "majorAxis": v(0.93, 0.38)});
            skEllipse(sketch, "E5.9.0.5", {"center": v(13.5, -8.15) * mm, "majorRadius": 0.17 * mm, "minorRadius": 0.12 * mm, "majorAxis": v(0.93, 0.38)});
            skEllipse(sketch, "E5.9.0.6", {"center": v(12.8, -8.15) * mm, "majorRadius": 0.17 * mm, "minorRadius": 0.12 * mm, "majorAxis": v(0.93, 0.38)});
            skEllipse(sketch, "E5.9.0.7", {"center": v(12.1, -8.15) * mm, "majorRadius": 0.17 * mm, "minorRadius": 0.12 * mm, "majorAxis": v(0.93, 0.38)});
            skEllipse(sketch, "E5.9.0.8", {"center": v(11.4, -8.15) * mm, "majorRadius": 0.17 * mm, "minorRadius": 0.12 * mm, "majorAxis": v(0.93, 0.38)});
            skEllipse(sketch, "E5.9.0.9", {"center": v(10.7, -8.15) * mm, "majorRadius": 0.17 * mm, "minorRadius": 0.12 * mm, "majorAxis": v(0.93, 0.38)});
            skEllipse(sketch, "E5.9.0.10", {"center": v(10, -8.15) * mm, "majorRadius": 0.17 * mm, "minorRadius": 0.12 * mm, "majorAxis": v(0.93, 0.38)});
            skEllipse(sketch, "E5.9.0.11", {"center": v(9.3, -8.15) * mm, "majorRadius": 0.17 * mm, "minorRadius": 0.12 * mm, "majorAxis": v(0.93, 0.38)});
            skEllipse(sketch, "E5.9.0.12", {"center": v(8.6, -8.15) * mm, "majorRadius": 0.17 * mm, "minorRadius": 0.12 * mm, "majorAxis": v(0.93, 0.38)});
            skEllipse(sketch, "E5.9.0.13", {"center": v(7.9, -8.15) * mm, "majorRadius": 0.17 * mm, "minorRadius": 0.12 * mm, "majorAxis": v(0.93, 0.38)});
            skEllipse(sketch, "E5.9.0.14", {"center": v(7.2, -8.15) * mm, "majorRadius": 0.17 * mm, "minorRadius": 0.12 * mm, "majorAxis": v(0.93, 0.38)});
            skEllipse(sketch, "E5.9.0.15", {"center": v(5.8, -8.15) * mm, "majorRadius": 0.17 * mm, "minorRadius": 0.12 * mm, "majorAxis": v(0.93, 0.38)});
            skEllipse(sketch, "E5.9.0.16", {"center": v(5.1, -8.15) * mm, "majorRadius": 0.17 * mm, "minorRadius": 0.12 * mm, "majorAxis": v(0.93, 0.38)});
            skEllipse(sketch, "E5.9.0.17", {"center": v(6.5, -8.15) * mm, "majorRadius": 0.17 * mm, "minorRadius": 0.12 * mm, "majorAxis": v(0.93, 0.38)});
            skEllipse(sketch, "E5.9.0.18", {"center": v(4.4, -8.15) * mm, "majorRadius": 0.17 * mm, "minorRadius": 0.12 * mm, "majorAxis": v(0.93, 0.38)});
            skEllipse(sketch, "E5.9.0.19", {"center": v(3.7, -8.15) * mm, "majorRadius": 0.17 * mm, "minorRadius": 0.12 * mm, "majorAxis": v(0.93, 0.38)});
            skEllipse(sketch, "E5.9.0.20", {"center": v(3, -8.15) * mm, "majorRadius": 0.17 * mm, "minorRadius": 0.12 * mm, "majorAxis": v(0.93, 0.38)});
            skLineSegment(sketch, "E5.direction1", {"start": v(17, -1.85) * mm, "end": v(17, -2.55) * mm, "construction": true});
            skSolve(sketch);
        }
        {
            var Q0;
            Q0=makeQuery(id+"F0.imprint","IMPRINT",FACE,{"disambiguationData":[TD([[makeQuery(id+"F0.imprint","IMPRINT",EDGE,{"derivedFrom":sQuery(id+"F0.wireOp",EDGE,"E0.bottom")}),-1.0]])]});
            extrude(context, id + "F1", {"entities" : qUnion([Q0]), "depth" : 0.2 * mm, "offsetDistance" : 25.4 * mm});
        }
    });
